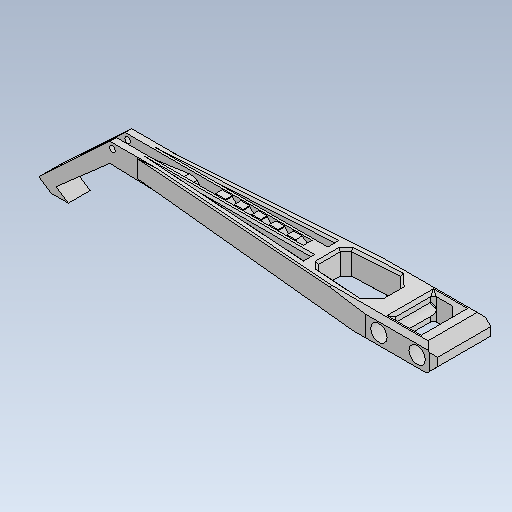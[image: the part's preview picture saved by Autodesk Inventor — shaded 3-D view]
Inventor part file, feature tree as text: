
AUTODESK INVENTOR PART (.ipt)
format: ipt  version: 2023 (Build 270158030, 158C)  size: 284,672 bytes
history: native  units: mm
features: other x4, chamfer x1
ambient origin geometry x8: Origin, YZ Plane, XZ Plane, XY Plane, X Axis, Y Axis, Z Axis, Center Point
bodies: Body1 (feature_tree)
feature tree (5):
  other  "V4.0-trebuchet-complete-parts.ipt"
  chamfer  "Chamfer1"  Distance=10.0mm
  other  "throw-arm-top::V4.0-trebuchet-complete-parts.ipt"
  other  "TaggingFeature1"
  other  "throw-arm-top"
